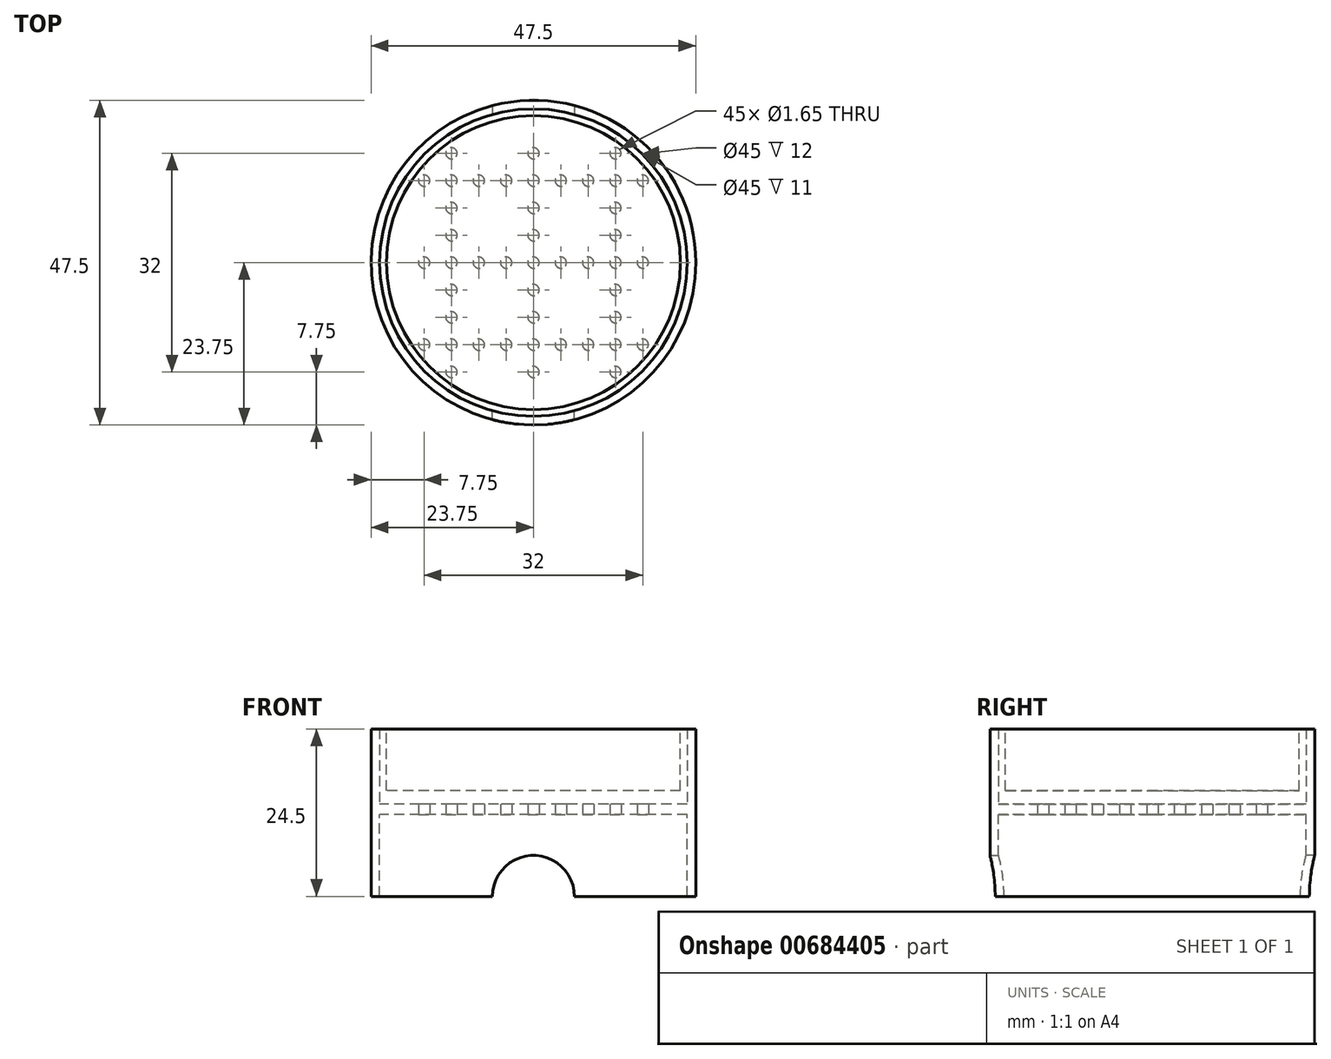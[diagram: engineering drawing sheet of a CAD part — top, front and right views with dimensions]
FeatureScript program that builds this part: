
annotation { "Feature Type Name" : "Feature", "Feature Type Description" : "" }
export const myFeature = defineFeature(function(context is Context, id is Id, definition is map)
    precondition{}
    {
        {
            var Q0;
            Q0=qCreatedBy(makeId("Top.planeOp"),FACE);
            var sketch = newSketch(context, id + "F0", { "sketchPlane" : qUnion([Q0])});
            skCircle(sketch, "E0", {"center": v(0, 0) * mm, "radius": 23.75 * mm});
            skCircle(sketch, "E1", {"center": v(0, 0) * mm, "radius": 22.5 * mm});
            skCircle(sketch, "E2", {"center": v(0, 0) * mm, "radius": 0.6 * mm, "construction": true});
            skLineSegment(sketch, "E3", {"start": v(-23.75, 0) * mm, "end": v(23.75, 0) * mm, "construction": true});
            skCircle(sketch, "E4", {"center": v(4, 0) * mm, "radius": 0.6 * mm, "construction": true});
            skCircle(sketch, "E5", {"center": v(-4, 0) * mm, "radius": 0.6 * mm, "construction": true});
            skCircle(sketch, "E6", {"center": v(0, 4) * mm, "radius": 0.6 * mm, "construction": true});
            skCircle(sketch, "E7", {"center": v(0, -4) * mm, "radius": 0.6 * mm, "construction": true});
            skCircle(sketch, "E8.1.0.0", {"center": v(12, 4) * mm, "radius": 0.6 * mm, "construction": true});
            skCircle(sketch, "E8.1.0.1", {"center": v(16, 0) * mm, "radius": 0.6 * mm, "construction": true});
            skCircle(sketch, "E8.1.0.2", {"center": v(12, -4) * mm, "radius": 0.6 * mm, "construction": true});
            skCircle(sketch, "E8.1.0.3", {"center": v(8, 0) * mm, "radius": 0.6 * mm, "construction": true});
            skCircle(sketch, "E8.1.0.4", {"center": v(12, 0) * mm, "radius": 0.6 * mm, "construction": true});
            skLineSegment(sketch, "E8.direction1", {"start": v(0, -4) * mm, "end": v(12, -4) * mm, "construction": true});
            skCircle(sketch, "E9.1.0.0", {"center": v(-12, 4) * mm, "radius": 0.6 * mm, "construction": true});
            skCircle(sketch, "E9.1.0.1", {"center": v(-16, 0) * mm, "radius": 0.6 * mm, "construction": true});
            skCircle(sketch, "E9.1.0.2", {"center": v(-12, -4) * mm, "radius": 0.6 * mm, "construction": true});
            skCircle(sketch, "E9.1.0.3", {"center": v(-8, 0) * mm, "radius": 0.6 * mm, "construction": true});
            skCircle(sketch, "E9.1.0.4", {"center": v(-12, 0) * mm, "radius": 0.6 * mm, "construction": true});
            skLineSegment(sketch, "E9.direction1", {"start": v(0, 0) * mm, "end": v(-12, 0) * mm, "construction": true});
            skLineSegment(sketch, "E10", {"start": v(0, 23.75) * mm, "end": v(0, -23.75) * mm, "construction": true});
            skCircle(sketch, "E11.1.0.0", {"center": v(-16, 12) * mm, "radius": 0.6 * mm, "construction": true});
            skCircle(sketch, "E11.1.0.1", {"center": v(-12, 8) * mm, "radius": 0.6 * mm, "construction": true});
            skCircle(sketch, "E11.1.0.2", {"center": v(-12, 12) * mm, "radius": 0.6 * mm, "construction": true});
            skCircle(sketch, "E11.1.0.3", {"center": v(-8, 12) * mm, "radius": 0.6 * mm, "construction": true});
            skCircle(sketch, "E11.1.0.4", {"center": v(-4, 12) * mm, "radius": 0.6 * mm, "construction": true});
            skCircle(sketch, "E11.1.0.5", {"center": v(0, 16) * mm, "radius": 0.6 * mm, "construction": true});
            skCircle(sketch, "E11.1.0.6", {"center": v(4, 12) * mm, "radius": 0.6 * mm, "construction": true});
            skCircle(sketch, "E11.1.0.7", {"center": v(0, 12) * mm, "radius": 0.6 * mm, "construction": true});
            skCircle(sketch, "E11.1.0.8", {"center": v(0, 8) * mm, "radius": 0.6 * mm, "construction": true});
            skCircle(sketch, "E11.1.0.9", {"center": v(8, 12) * mm, "radius": 0.6 * mm, "construction": true});
            skCircle(sketch, "E11.1.0.10", {"center": v(12, 12) * mm, "radius": 0.6 * mm, "construction": true});
            skCircle(sketch, "E11.1.0.11", {"center": v(16, 12) * mm, "radius": 0.6 * mm, "construction": true});
            skCircle(sketch, "E11.1.0.12", {"center": v(12, 8) * mm, "radius": 0.6 * mm, "construction": true});
            skCircle(sketch, "E11.1.0.13", {"center": v(12, 16) * mm, "radius": 0.6 * mm, "construction": true});
            skCircle(sketch, "E11.1.0.14", {"center": v(-12, 16) * mm, "radius": 0.6 * mm, "construction": true});
            skLineSegment(sketch, "E11.direction1", {"start": v(0, 0) * mm, "end": v(0, 12) * mm, "construction": true});
            skCircle(sketch, "E12.1.0.0", {"center": v(-16, -12) * mm, "radius": 0.6 * mm, "construction": true});
            skCircle(sketch, "E12.1.0.1", {"center": v(-12, -16) * mm, "radius": 0.6 * mm, "construction": true});
            skCircle(sketch, "E12.1.0.2", {"center": v(-12, -12) * mm, "radius": 0.6 * mm, "construction": true});
            skCircle(sketch, "E12.1.0.3", {"center": v(-12, -8) * mm, "radius": 0.6 * mm, "construction": true});
            skCircle(sketch, "E12.1.0.4", {"center": v(-8, -12) * mm, "radius": 0.6 * mm, "construction": true});
            skCircle(sketch, "E12.1.0.5", {"center": v(-4, -12) * mm, "radius": 0.6 * mm, "construction": true});
            skCircle(sketch, "E12.1.0.6", {"center": v(0, -8) * mm, "radius": 0.6 * mm, "construction": true});
            skCircle(sketch, "E12.1.0.7", {"center": v(0, -12) * mm, "radius": 0.6 * mm, "construction": true});
            skCircle(sketch, "E12.1.0.8", {"center": v(0, -16) * mm, "radius": 0.6 * mm, "construction": true});
            skCircle(sketch, "E12.1.0.9", {"center": v(4, -12) * mm, "radius": 0.6 * mm, "construction": true});
            skCircle(sketch, "E12.1.0.10", {"center": v(8, -12) * mm, "radius": 0.6 * mm, "construction": true});
            skCircle(sketch, "E12.1.0.11", {"center": v(12, -12) * mm, "radius": 0.6 * mm, "construction": true});
            skCircle(sketch, "E12.1.0.12", {"center": v(16, -12) * mm, "radius": 0.6 * mm, "construction": true});
            skCircle(sketch, "E12.1.0.13", {"center": v(12, -8) * mm, "radius": 0.6 * mm, "construction": true});
            skCircle(sketch, "E12.1.0.14", {"center": v(12, -16) * mm, "radius": 0.6 * mm, "construction": true});
            skLineSegment(sketch, "E12.direction1", {"start": v(0, 0) * mm, "end": v(0, -12) * mm, "construction": true});
            skSolve(sketch);
        }
        {
            var Q0;
            Q0=makeQuery(id+"F0.imprint","IMPRINT",FACE,{"disambiguationData":[TD([[makeQuery(id+"F0.imprint","IMPRINT",EDGE,{"derivedFrom":sQuery(id+"F0.wireOp",EDGE,"E0")}),1.0]])]});
            extrude(context, id + "F1", {"entities" : qUnion([Q0]), "depth" : 12.5 * mm, "offsetDistance" : 25 * mm});
        }
        {
            var Q0;
            Q0=makeQuery(id+"F0.imprint","IMPRINT",FACE,{"disambiguationData":[TD([[makeQuery(id+"F0.imprint","IMPRINT",EDGE,{"derivedFrom":sQuery(id+"F0.wireOp",EDGE,"E1")}),1.0]])]});
            extrude(context, id + "F2", {"entities" : qUnion([Q0]), "operationType" : NewBodyOperationType.ADD, "depth" : 1.5 * mm, "offsetDistance" : 25 * mm});
        }
        {
            var Q0;
            Q0=sQuery(id+"F0.wireOp",VERTEX,"E11.1.0.0.center");
            var Q1;
            Q1=sQuery(id+"F0.wireOp",VERTEX,"E9.1.0.1.center");
            var Q2;
            Q2=sQuery(id+"F0.wireOp",VERTEX,"E9.direction1.end");
            var Q3;
            Q3=sQuery(id+"F0.wireOp",VERTEX,"E9.1.0.2.center");
            var Q4;
            Q4=sQuery(id+"F0.wireOp",VERTEX,"E9.1.0.0.center");
            var Q5;
            Q5=sQuery(id+"F0.wireOp",VERTEX,"E11.1.0.1.center");
            var Q6;
            Q6=sQuery(id+"F0.wireOp",VERTEX,"E11.1.0.2.center");
            var Q7;
            Q7=sQuery(id+"F0.wireOp",VERTEX,"E11.1.0.14.center");
            var Q8;
            Q8=sQuery(id+"F0.wireOp",VERTEX,"E11.1.0.3.center");
            var Q9;
            Q9=sQuery(id+"F0.wireOp",VERTEX,"E12.1.0.1.center");
            var Q10;
            Q10=sQuery(id+"F0.wireOp",VERTEX,"E12.1.0.2.center");
            var Q11;
            Q11=sQuery(id+"F0.wireOp",VERTEX,"E12.1.0.0.center");
            var Q12;
            Q12=sQuery(id+"F0.wireOp",VERTEX,"E12.1.0.4.center");
            var Q13;
            Q13=sQuery(id+"F0.wireOp",VERTEX,"E12.1.0.3.center");
            var Q14;
            Q14=sQuery(id+"F0.wireOp",VERTEX,"E12.1.0.5.center");
            var Q15;
            Q15=sQuery(id+"F0.wireOp",VERTEX,"E12.1.0.8.center");
            var Q16;
            Q16=sQuery(id+"F0.wireOp",VERTEX,"E12.direction1.end");
            var Q17;
            Q17=sQuery(id+"F0.wireOp",VERTEX,"E12.1.0.6.center");
            var Q18;
            Q18=sQuery(id+"F0.wireOp",VERTEX,"E12.1.0.9.center");
            var Q19;
            Q19=sQuery(id+"F0.wireOp",VERTEX,"E12.1.0.10.center");
            var Q20;
            Q20=sQuery(id+"F0.wireOp",VERTEX,"E7.center");
            var Q21;
            Q21=sQuery(id+"F0.wireOp",VERTEX,"E5.center");
            var Q22;
            Q22=sQuery(id+"F0.wireOp",VERTEX,"E9.1.0.3.center");
            var Q23;
            Q23=sQuery(id+"F0.wireOp",VERTEX,"E6.center");
            var Q24;
            Q24=sQuery(id+"F0.wireOp",VERTEX,"E4.center");
            var Q25;
            Q25=sQuery(id+"F0.wireOp",VERTEX,"E0.center");
            var Q26;
            Q26=sQuery(id+"F0.wireOp",VERTEX,"E11.1.0.8.center");
            var Q27;
            Q27=sQuery(id+"F0.wireOp",VERTEX,"E11.1.0.4.center");
            var Q28;
            Q28=sQuery(id+"F0.wireOp",VERTEX,"E11.direction1.end");
            var Q29;
            Q29=sQuery(id+"F0.wireOp",VERTEX,"E11.1.0.5.center");
            var Q30;
            Q30=sQuery(id+"F0.wireOp",VERTEX,"E11.1.0.6.center");
            var Q31;
            Q31=sQuery(id+"F0.wireOp",VERTEX,"E11.1.0.9.center");
            var Q32;
            Q32=sQuery(id+"F0.wireOp",VERTEX,"E11.1.0.13.center");
            var Q33;
            Q33=sQuery(id+"F0.wireOp",VERTEX,"E11.1.0.10.center");
            var Q34;
            Q34=sQuery(id+"F0.wireOp",VERTEX,"E11.1.0.11.center");
            var Q35;
            Q35=sQuery(id+"F0.wireOp",VERTEX,"E11.1.0.12.center");
            var Q36;
            Q36=sQuery(id+"F0.wireOp",VERTEX,"E8.1.0.0.center");
            var Q37;
            Q37=sQuery(id+"F0.wireOp",VERTEX,"E8.1.0.4.center");
            var Q38;
            Q38=sQuery(id+"F0.wireOp",VERTEX,"E8.1.0.3.center");
            var Q39;
            Q39=sQuery(id+"F0.wireOp",VERTEX,"E8.1.0.1.center");
            var Q40;
            Q40=sQuery(id+"F0.wireOp",VERTEX,"E8.direction1.end");
            var Q41;
            Q41=sQuery(id+"F0.wireOp",VERTEX,"E12.1.0.13.center");
            var Q42;
            Q42=sQuery(id+"F0.wireOp",VERTEX,"E12.1.0.12.center");
            var Q43;
            Q43=sQuery(id+"F0.wireOp",VERTEX,"E12.1.0.11.center");
            var Q44;
            Q44=sQuery(id+"F0.wireOp",VERTEX,"E12.1.0.14.center");
            var Q45;
            Q45=makeQuery(id+"F1.opExtrude","SWEPT_BODY",BODY,{"disambiguationData":[OSD([sQuery(id+"F0.wireOp",EDGE,"E0"),sQuery(id+"F0.wireOp",EDGE,"E1")])]});
            hole(context, id + "F3", {"style" : HoleStyle.SIMPLE, "endStyle" : HoleEndStyle.THROUGH, "oppositeDirection" : true, "holeDiameter" : 1.65 * mm, "majorDiameter" : 5 * mm, "isTappedThrough" : true, "tappedDepth" : 12 * mm, "tapClearance" : 3, "locations" : qUnion([Q0, Q1, Q2, Q3, Q4, Q5, Q6, Q7, Q8, Q9, Q10, Q11, Q12, Q13, Q14, Q15, Q16, Q17, Q18, Q19, Q20, Q21, Q22, Q23, Q24, Q25, Q26, Q27, Q28, Q29, Q30, Q31, Q32, Q33, Q34, Q35, Q36, Q37, Q38, Q39, Q40, Q41, Q42, Q43, Q44]), "scope" : qUnion([Q45])});
        }
        {
            var Q0;
            Q0=makeQuery(id+"F0.imprint","IMPRINT",FACE,{"disambiguationData":[TD([[makeQuery(id+"F0.imprint","IMPRINT",EDGE,{"derivedFrom":sQuery(id+"F0.wireOp",EDGE,"E0")}),1.0]])]});
            extrude(context, id + "F4", {"entities" : qUnion([Q0]), "operationType" : NewBodyOperationType.ADD, "oppositeDirection" : true, "depth" : 12 * mm, "offsetDistance" : 25 * mm});
        }
        {
            var Q0;
            Q0=qCreatedBy(makeId("Front.planeOp"),FACE);
            var sketch = newSketch(context, id + "F5", { "sketchPlane" : qUnion([Q0])});
            skCircle(sketch, "E13", {"center": v(0, -12) * mm, "radius": 6 * mm, "construction": true});
            skSolve(sketch);
        }
        {
            var Q0;
            Q0=sQuery(id+"F5.wireOp",VERTEX,"E13.center");
            var Q1;
            Q1=makeQuery(id+"F1.opExtrude","SWEPT_BODY",BODY,{"disambiguationData":[OSD([sQuery(id+"F0.wireOp",EDGE,"E0"),sQuery(id+"F0.wireOp",EDGE,"E1")])]});
            hole(context, id + "F6", {"style" : HoleStyle.SIMPLE, "endStyle" : HoleEndStyle.THROUGH, "oppositeDirection" : true, "holeDiameter" : 12 * mm, "majorDiameter" : 5 * mm, "isTappedThrough" : true, "tappedDepth" : 12 * mm, "tapClearance" : 3, "locations" : qUnion([Q0]), "scope" : qUnion([Q1])});
        }
        {
            var Q0;
            Q0=sQuery(id+"F5.wireOp",VERTEX,"E13.center");
            var Q1;
            Q1=makeQuery(id+"F1.opExtrude","SWEPT_BODY",BODY,{"disambiguationData":[OSD([sQuery(id+"F0.wireOp",EDGE,"E0"),sQuery(id+"F0.wireOp",EDGE,"E1")])]});
            hole(context, id + "F7", {"style" : HoleStyle.SIMPLE, "endStyle" : HoleEndStyle.THROUGH, "holeDiameter" : 12 * mm, "majorDiameter" : 5 * mm, "isTappedThrough" : true, "tappedDepth" : 12 * mm, "tapClearance" : 3, "locations" : qUnion([Q0]), "scope" : qUnion([Q1])});
        }
        {
            var Q0;
            Q0=makeQuery(id+"F1.opExtrude","CAP_FACE",FACE,{"disambiguationData":[OSD([sQuery(id+"F0.wireOp",EDGE,"E0"),sQuery(id+"F0.wireOp",EDGE,"E1")])],"isStart":false});
            var sketch = newSketch(context, id + "F8", { "sketchPlane" : qUnion([Q0])});
            skCircle(sketch, "E14.0", {"center": v(0, 0) * mm, "radius": 21.5 * mm});
            skSolve(sketch);
        }
        {
            var Q0;
            Q0 = qSketchRegion(id + "F8", true);
            var Q1;
            Q1=makeQuery(id+"F2.opExtrude","CAP_FACE",FACE,{"disambiguationData":[OSD([sQuery(id+"F0.wireOp",EDGE,"E1")])],"isStart":false});
            extrude(context, id + "F9", {"entities" : qUnion([Q0]), "endBound" : BoundingType.UP_TO_SURFACE, "oppositeDirection" : true, "depth" : 25 * mm, "endBoundEntityFace" : qUnion([Q1]), "hasOffset" : true, "offsetDistance" : 2 * mm});
        }
    });
